# Revit family: Faucet-Deck_Mount-Bath-KALLISTA-Aileron-P33349
name_source: partatom
category: Plumbing Fixtures
units: mm (PartAtom-declared; Revit-internal decimal feet)

## family parameters
Cut with Voids When Loaded = No
Host = Face
OmniClass Number = 23.31.11.00
OmniClass Title = Faucets
Part Type = Normal
Room Calculation Point = No
Round Connector Dimension = Use Diameter
Shared = No

## types (6) — shared parameters
ADA Compliant = No
Assembly Code = D2010
CW Connection = Yes
Cold Water Inlet = Cold Water Inlet
Date Modified = 10/22/2024
Default Elevation = 36"
Description = With Desperad Sink Faucet,Standard
Drain Included = Yes
Flow Rate = 1 GPM
HW Connection = Yes
Handle Clearance = 2 5/8"
Height = 6 15/16"
Hot Water Inlet = Hot Water Inlet
Length = 6 1/8"
Manufacturer = Kallista Co.
Master Format 2014 = 22 41 39
Master Format 2014 Name = Residential Faucets, Supplies, and Trim
Material = Premium Metal Construction
Pressure = 4.50 psi
Product Name = Aileron
Spout Reach = 6 1/8"
URL = https://www.kallista.com
Vent Connection = No
Waste Connection = No
Waste Water Outlet = Waste Water Outlet
WaterSense Certified = No

## per-type parameters (varying)
| type | Finish | Model | Type |
| 2MB-Brushed Brass | Kallista-Metal-2MB- Brushed_Brass | P-33349-LV-2MB | 1 |
| BGP-Brushed Graphite | Kallista-Metal-BGP-Brushed_Graphite | P-33349-LV-BGP | 2 |
| BL-Matte Black | Kallista-Metal-BL-Matte_Black | P-33349-LV-BL | 3 |
| BLH-Blush Brass | Kallista-Metal-BLH-Blush_Brass | P-33349-LV-BLH | 4 |
| BN-Brushed Nickel | Kallista-Metal-BN-Brushed_Nickel | P-33349-LV-BN | 5 |
| CP-Chrome | Kallista-Metal-CP-Chrome | P-33349-LV-CP | 6 |

## geometry (parser evidence)
native form markers: Sweep x9
no freeform markers — native parametric forms only
